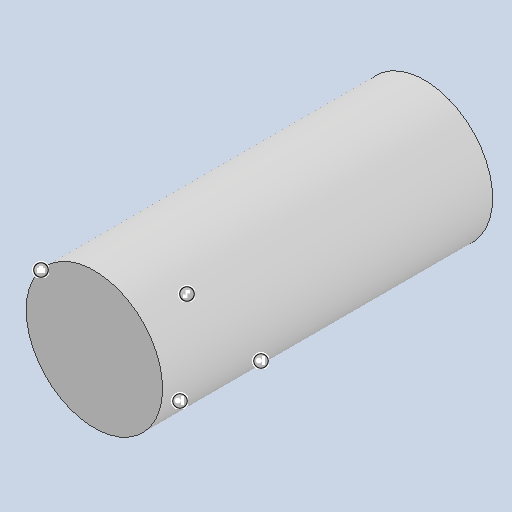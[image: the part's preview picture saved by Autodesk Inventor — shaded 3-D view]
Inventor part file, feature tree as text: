
AUTODESK INVENTOR PART (.ipt)
format: ipt  version: 2025 (Build 290162000, 162)  size: 205,312 bytes
history: native  units: mm
features: extrude x1
ambient origin geometry x8: Origin, YZ Plane, XZ Plane, XY Plane, X Axis, Y Axis, Z Axis, Center Point
bodies: Solid1 (feature_tree)
feature tree (1):
  extrude  "Extrusion1"  TaperAngle=0.0deg  [1 undecoded]
note: 1 required parameter value undecoded (feature->parameter linkage not recoverable at this tier; creation-order binding heuristic only, values carry confidence <= 0.55)
